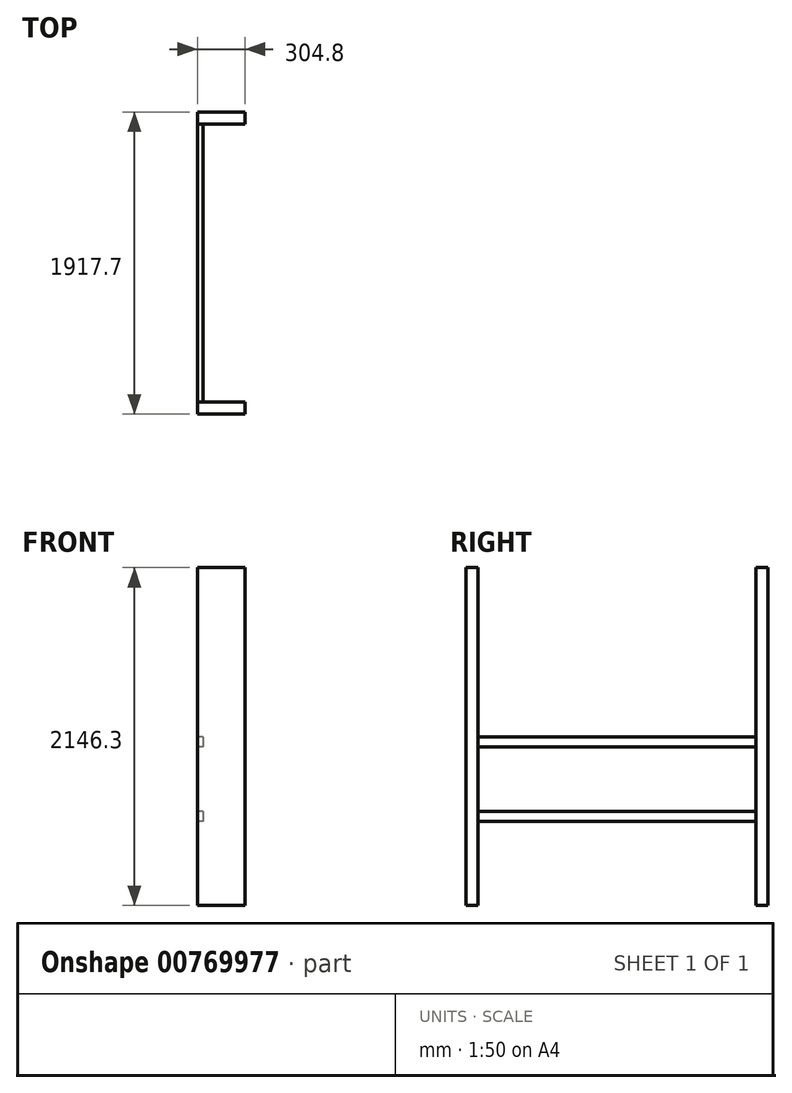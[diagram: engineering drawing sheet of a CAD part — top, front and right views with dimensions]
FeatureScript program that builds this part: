
annotation { "Feature Type Name" : "Feature", "Feature Type Description" : "" }
export const myFeature = defineFeature(function(context is Context, id is Id, definition is map)
    precondition{}
    {
        {
            var Q0;
            Q0=qCreatedBy(makeId("Right.planeOp"),FACE);
            var sketch = newSketch(context, id + "F0", { "sketchPlane" : qUnion([Q0])});
            skLineSegment(sketch, "E0.bottom", {"start": v(-640.28, -723.87) * mm, "end": v(1125.02, -723.87) * mm});
            skLineSegment(sketch, "E0.top", {"start": v(-640.28, -787.37) * mm, "end": v(1125.02, -787.37) * mm});
            skLineSegment(sketch, "E0.left", {"start": v(-640.28, -723.87) * mm, "end": v(-640.28, -787.37) * mm});
            skLineSegment(sketch, "E0.right", {"start": v(1125.02, -723.87) * mm, "end": v(1125.02, -787.37) * mm});
            skLineSegment(sketch, "E1.bottom", {"start": v(-640.28, -1198.9) * mm, "end": v(1125.02, -1198.9) * mm});
            skLineSegment(sketch, "E1.top", {"start": v(-640.28, -1262.4) * mm, "end": v(1125.02, -1262.4) * mm});
            skLineSegment(sketch, "E1.left", {"start": v(-640.28, -1198.9) * mm, "end": v(-640.28, -1262.4) * mm});
            skLineSegment(sketch, "E1.right", {"start": v(1125.02, -1198.9) * mm, "end": v(1125.02, -1262.4) * mm});
            skSolve(sketch);
        }
        {
            var Q0;
            Q0 = qSketchRegion(id + "F0", true);
            extrude(context, id + "F1", {"entities" : qUnion([Q0]), "depth" : 38.1 * mm, "offsetDistance" : 25.4 * mm});
        }
        {
            var Q0;
            Q0=makeQuery(id+"F1.opExtrude","CAP_FACE",FACE,{"disambiguationData":[OSD([sQuery(id+"F0.wireOp",EDGE,"E0.bottom"),sQuery(id+"F0.wireOp",EDGE,"E0.top"),sQuery(id+"F0.wireOp",EDGE,"E0.left"),sQuery(id+"F0.wireOp",EDGE,"E0.right")])],"isStart":true});
            var sketch = newSketch(context, id + "F2", { "sketchPlane" : qUnion([Q0])});
            skLineSegment(sketch, "E2.bottom", {"start": v(716.48, 350.5) * mm, "end": v(640.28, 350.5) * mm});
            skLineSegment(sketch, "E2.top", {"start": v(716.48, -1795.8) * mm, "end": v(640.28, -1795.8) * mm});
            skLineSegment(sketch, "E2.left", {"start": v(716.48, 350.5) * mm, "end": v(716.48, -1795.8) * mm});
            skLineSegment(sketch, "E2.right", {"start": v(640.28, 350.5) * mm, "end": v(640.28, -1795.8) * mm});
            skLineSegment(sketch, "E3.bottom", {"start": v(-1125.02, -1795.8) * mm, "end": v(-1201.22, -1795.8) * mm});
            skLineSegment(sketch, "E3.top", {"start": v(-1125.02, 350.5) * mm, "end": v(-1201.22, 350.5) * mm});
            skLineSegment(sketch, "E3.left", {"start": v(-1125.02, -1795.8) * mm, "end": v(-1125.02, 350.5) * mm});
            skLineSegment(sketch, "E3.right", {"start": v(-1201.22, -1795.8) * mm, "end": v(-1201.22, 350.5) * mm});
            skSolve(sketch);
        }
        {
            var Q0;
            Q0 = qSketchRegion(id + "F2", true);
            extrude(context, id + "F3", {"entities" : qUnion([Q0]), "oppositeDirection" : true, "depth" : 304.8 * mm, "offsetDistance" : 25.4 * mm});
        }
    });
